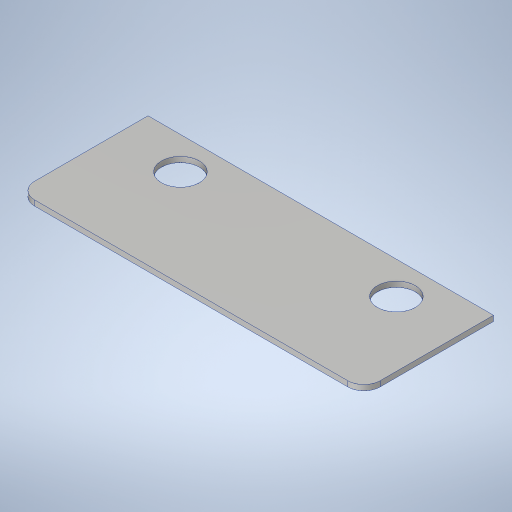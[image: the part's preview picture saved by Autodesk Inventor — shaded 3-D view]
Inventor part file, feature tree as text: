
AUTODESK INVENTOR PART (.ipt)
format: ipt  version: 2023.4 (Build 274418000, 418)  size: 237,056 bytes
history: native  units: in
note: dims shown in document units (in); Inventor stores cm internally (conversion verified against a paired STEP export)
features: sketch x2, extrude x1, hole x1, fillet x1
ambient origin geometry x8: Origin, YZ Plane, XZ Plane, XY Plane, X Axis, Y Axis, Z Axis, Center Point
bodies: Solid1 (feature_tree)
feature tree (5):
  extrude  "Extrusion1"  Depth=3.0in
  hole  "Hole1"  [1 undecoded]
  fillet  "Fillet1"  Radius=2.5in
  sketch  "Sketch1"  dims[d0=8.0in d1=3.0in]
  sketch  "Sketch2"  dims[d2=0.125in d3=0.0in d4=0.75in d5=2.5in d6=0.875in d7=0.75in d8=0.375in d9=0.25in d10=0.5635in d11=1.0in d12=0.8108in d13=0.375in]
note: 1 required parameter value undecoded (feature->parameter linkage not recoverable at this tier; creation-order binding heuristic only, values carry confidence <= 0.55)
